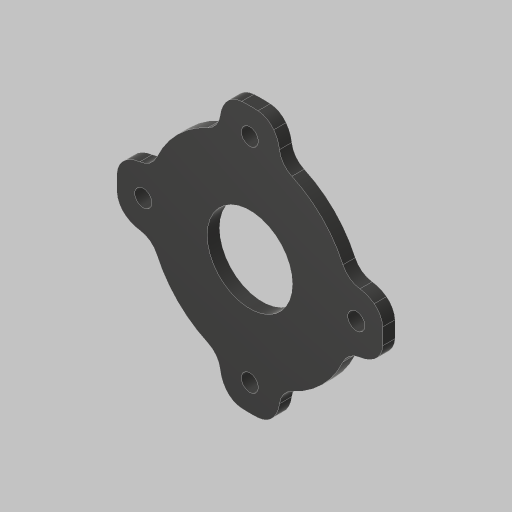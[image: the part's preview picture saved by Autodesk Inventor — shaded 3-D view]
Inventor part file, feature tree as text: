
AUTODESK INVENTOR PART (.ipt)
format: ipt  version: 2023.5 (Build 275446000, 446)  size: 183,296 bytes
history: native  units: in
note: dims shown in document units (in); Inventor stores cm internally (conversion verified against a paired STEP export)
features: extrude x3, sketch x2, hole x1, mirror x1, fillet x1, projected_geometry x1
ambient origin geometry x8: Origin, YZ Plane, XZ Plane, XY Plane, X Axis, Y Axis, Z Axis, Center Point
bodies: Solid1 (feature_tree)
feature tree (9):
  sketch  "Sketch1"  dims[d0=1.875in d1=0.625in]
  extrude  "Extrusion1"  Depth=0.625in
  extrude  "Extrusion2"  Depth=0.145in TaperAngle=0.0deg
  hole  "Hole1"  [1 undecoded]
  extrude  "Extrusion3"  Depth=0.25in TaperAngle=0.0deg
  mirror  "Mirror1"
  fillet  "Fillet1"  Radius=0.25in
  sketch  "Sketch2"  dims[d2=2.5in d3=0.145in d4=0.0in d5=1.0in d6=0.25in d7=0.0in d8=0.201in d9=0.38in d10=0.385in d11=0.25in d12=0.5635in d13=1.0in d14=0.8108in d15=0.25in d16=0.25in d18=0.25in d19=0.25in d20=45.0deg d21=0.25in d22=45.0deg d23=0.25in d24=0.0in d25=0.25in d26=0.25in d27=0.25in]
  projected_geometry  "Project Cut Edges1"
note: 1 required parameter value undecoded (feature->parameter linkage not recoverable at this tier; creation-order binding heuristic only, values carry confidence <= 0.55)
